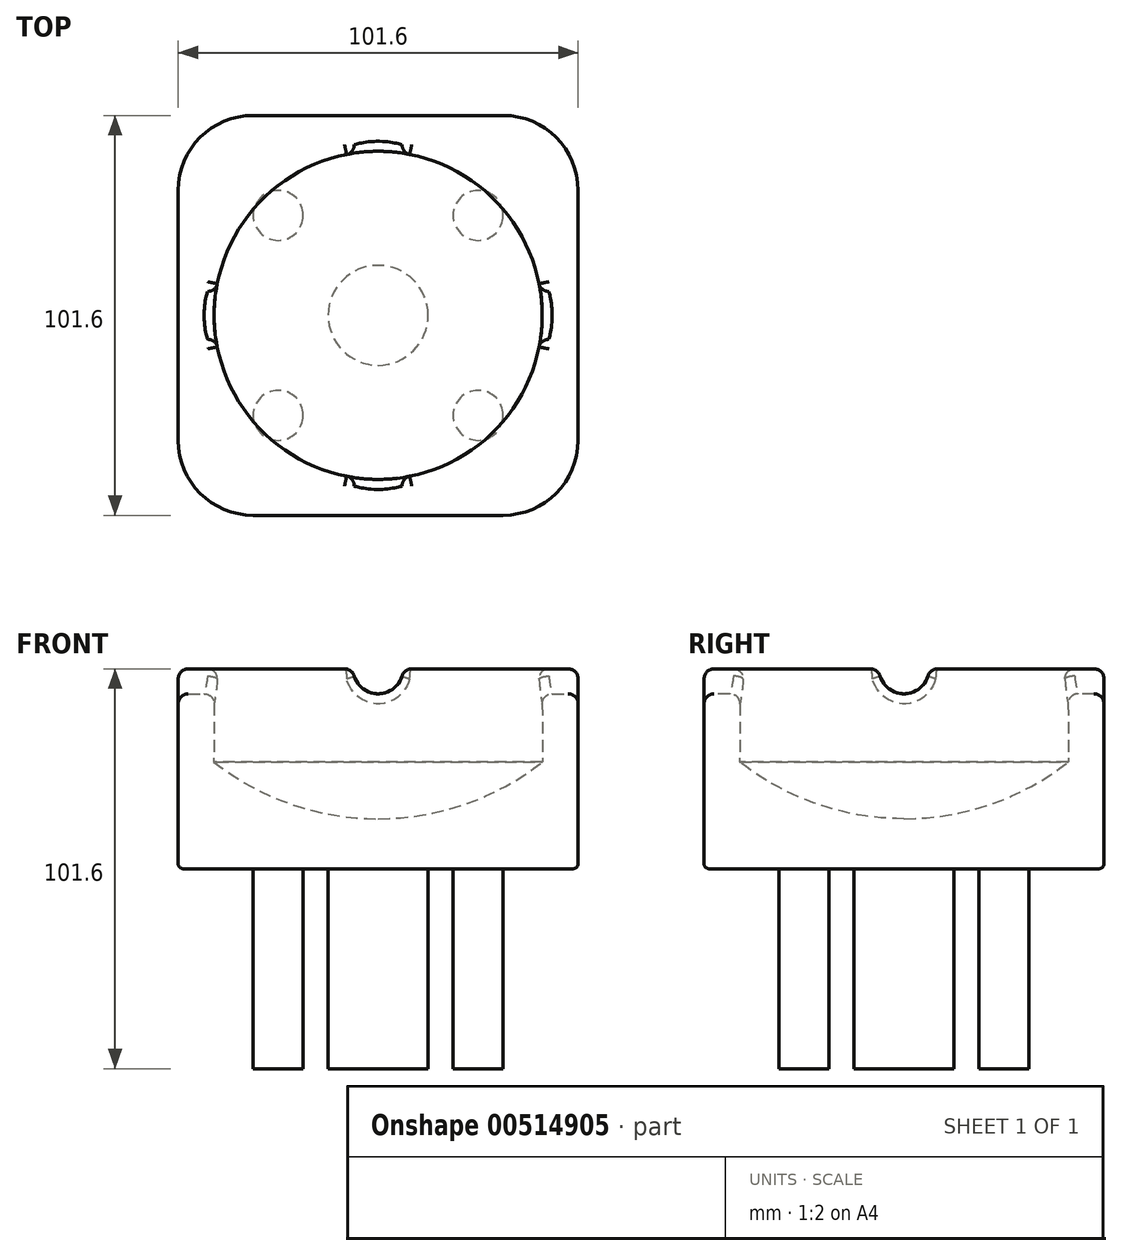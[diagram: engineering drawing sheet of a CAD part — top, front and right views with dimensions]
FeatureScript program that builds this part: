
annotation { "Feature Type Name" : "Feature", "Feature Type Description" : "" }
export const myFeature = defineFeature(function(context is Context, id is Id, definition is map)
    precondition{}
    {
        {
            var Q0;
            Q0=qCreatedBy(makeId("Top.planeOp"),FACE);
            var sketch = newSketch(context, id + "F0", { "sketchPlane" : qUnion([Q0])});
            skLineSegment(sketch, "E0.bottom", {"start": v(50.8, -50.8) * mm, "end": v(-50.8, -50.8) * mm});
            skLineSegment(sketch, "E0.top", {"start": v(50.8, 50.8) * mm, "end": v(-50.8, 50.8) * mm});
            skLineSegment(sketch, "E0.left", {"start": v(50.8, -50.8) * mm, "end": v(50.8, 50.8) * mm});
            skLineSegment(sketch, "E0.right", {"start": v(-50.8, -50.8) * mm, "end": v(-50.8, 50.8) * mm});
            skPoint(sketch, "E0.middle", {"position": v(0, 0) * mm});
            skSolve(sketch);
        }
        {
            var Q0;
            Q0 = qSketchRegion(id + "F0", true);
            extrude(context, id + "F1", {"entities" : qUnion([Q0]), "depth" : 50.8 * mm, "offsetDistance" : 25.4 * mm});
        }
        {
            var Q0;
            Q0=qCreatedBy(makeId("Right.planeOp"),FACE);
            var sketch = newSketch(context, id + "F2", { "sketchPlane" : qUnion([Q0])});
            skLineSegment(sketch, "E1", {"start": v(0, 0) * mm, "end": v(0, 27.14) * mm});
            skArc(sketch, "E2", {"start": v(0, 12.7) * mm, "mid": v(22.1, 16.41) * mm, "end": v(41.75, 27.14) * mm});
            skLineSegment(sketch, "E3", {"start": v(0, 27.14) * mm, "end": v(41.75, 27.14) * mm, "construction": true});
            skLineSegment(sketch, "E4", {"start": v(41.6, 56.83) * mm, "end": v(41.75, 27.14) * mm});
            skLineSegment(sketch, "E5", {"start": v(0, 12.7) * mm, "end": v(0, 56.83) * mm});
            skLineSegment(sketch, "E6", {"start": v(0, 56.83) * mm, "end": v(41.6, 56.83) * mm});
            skSolve(sketch);
        }
        {
            var Q0;
            Q0 = qSketchRegion(id + "F2", true);
            var Q1;
            Q1=sQuery(id+"F2.wireOp",EDGE,"E5");
            revolve(context, id + "F3", {"operationType" : NewBodyOperationType.REMOVE, "entities" : qUnion([Q0]), "axis" : qUnion([Q1]), "revolveType" : RevolveType.FULL, "oppositeDirection" : true});
        }
        {
            var Q0;
            Q0=makeQuery(id+"F1.opExtrude","SWEPT_FACE",FACE,{"disambiguationData":[OSD([sQuery(id+"F0.wireOp",EDGE,"E0.bottom")])]});
            var sketch = newSketch(context, id + "F4", { "sketchPlane" : qUnion([Q0])});
            skCircle(sketch, "E7", {"center": v(0, 50.8) * mm, "radius": 6.35 * mm});
            skSolve(sketch);
        }
        {
            var Q0;
            Q0 = qSketchRegion(id + "F4", true);
            extrude(context, id + "F5", {"entities" : qUnion([Q0]), "operationType" : NewBodyOperationType.REMOVE, "oppositeDirection" : true, "depth" : 381 * mm, "offsetDistance" : 25.4 * mm});
        }
        {
            var Q0;
            Q0=makeQuery(id+"F1.opExtrude","SWEPT_FACE",FACE,{"disambiguationData":[OSD([sQuery(id+"F0.wireOp",EDGE,"E0.left")])]});
            var sketch = newSketch(context, id + "F6", { "sketchPlane" : qUnion([Q0])});
            skCircle(sketch, "E8", {"center": v(0, 50.8) * mm, "radius": 6.35 * mm});
            skSolve(sketch);
        }
        {
            var Q0;
            {var subQ0=sQuery(id+"F6.wireOp",EDGE,"E8");var subQ1=makeQuery(id+"F1.opExtrude","CAP_EDGE",EDGE,{"disambiguationData":[OSD([sQuery(id+"F0.wireOp",EDGE,"E0.left")])],"isStart":false});var subQ2=makeQuery(id+"F6.imprint","INTERSECT",VERTEX,{"disambiguationData":[OD(0.0)],"derivedFrom":[subQ1,subQ0]});Q0=makeQuery(id+"F6.imprint","IMPRINT",FACE,{"disambiguationData":[TD([[makeQuery(id+"F6.imprint","IMPRINT",EDGE,{"disambiguationData":[TD([[subQ2,1.0]])],"derivedFrom":subQ0}),1.0]])]});}
            var Q1;
            {var subQ0=sQuery(id+"F6.wireOp",EDGE,"E8");var subQ1=makeQuery(id+"F1.opExtrude","CAP_EDGE",EDGE,{"disambiguationData":[OSD([sQuery(id+"F0.wireOp",EDGE,"E0.left")])],"isStart":false});var subQ2=makeQuery(id+"F6.imprint","INTERSECT",VERTEX,{"disambiguationData":[OD(0.0)],"derivedFrom":[subQ1,subQ0]});Q1=makeQuery(id+"F6.imprint","IMPRINT",FACE,{"disambiguationData":[TD([[makeQuery(id+"F6.imprint","IMPRINT",EDGE,{"disambiguationData":[TD([[subQ2,-1.0]])],"derivedFrom":subQ0}),1.0]])]});}
            extrude(context, id + "F7", {"entities" : qUnion([Q0, Q1]), "operationType" : NewBodyOperationType.REMOVE, "oppositeDirection" : true, "depth" : 127 * mm, "offsetDistance" : 25.4 * mm});
        }
        {
            var Q0;
            Q0=makeQuery(id+"F1.opExtrude","SWEPT_EDGE",EDGE,{"disambiguationData":[OSD([sQuery(id+"F0.wireOp",EDGE,"E0.bottom"),sQuery(id+"F0.wireOp",EDGE,"E0.left")])]});
            var Q1;
            Q1=makeQuery(id+"F1.opExtrude","SWEPT_EDGE",EDGE,{"disambiguationData":[OSD([sQuery(id+"F0.wireOp",EDGE,"E0.top"),sQuery(id+"F0.wireOp",EDGE,"E0.left")])]});
            var Q2;
            Q2=makeQuery(id+"F1.opExtrude","SWEPT_EDGE",EDGE,{"disambiguationData":[OSD([sQuery(id+"F0.wireOp",EDGE,"E0.top"),sQuery(id+"F0.wireOp",EDGE,"E0.right")])]});
            var Q3;
            Q3=makeQuery(id+"F1.opExtrude","SWEPT_EDGE",EDGE,{"disambiguationData":[OSD([sQuery(id+"F0.wireOp",EDGE,"E0.bottom"),sQuery(id+"F0.wireOp",EDGE,"E0.right")])]});
            fillet(context, id + "F8", {"entities" : qUnion([Q0, Q1, Q2, Q3]), "radius" : 19.05 * mm, "tangentPropagation" : true, "allowEdgeOverflow" : false});
        }
        {
            var Q0;
            {var subQ0=sQuery(id+"F0.wireOp",EDGE,"E0.bottom");var subQ1=makeQuery(id+"F1.opExtrude","SWEPT_FACE",FACE,{"disambiguationData":[OSD([subQ0])]});var subQ3=sQuery(id+"F0.wireOp",EDGE,"E0.right");var subQ4=sQuery(id+"F0.wireOp",EDGE,"E0.top");var subQ5=makeQuery(id+"F1.opExtrude","CAP_FACE",FACE,{"disambiguationData":[OSD([subQ0,subQ4,sQuery(id+"F0.wireOp",EDGE,"E0.left"),subQ3])],"isStart":false});var subQ7=makeQuery(id+"F1.opExtrude","SWEPT_FACE",FACE,{"disambiguationData":[OSD([subQ3])]});Q0=makeQuery(id+"F8.opFillet","BLEND_EDGE",EDGE,{"blendedFrom":[makeQuery(id+"F1.opExtrude","SWEPT_EDGE",EDGE,{"disambiguationData":[OSD([subQ0,subQ3])]}),makeQuery(id+"F7.boolean.opBoolean","SPLIT",FACE,{"disambiguationData":[TD([subQ1])],"derivedFrom":makeQuery(id+"F5.boolean.opBoolean","SPLIT",FACE,{"disambiguationData":[TD([subQ7])],"derivedFrom":subQ5})})],"blendedInto":[makeQuery(id+"F7.boolean.opBoolean","SPLIT",FACE,{"disambiguationData":[TD([subQ1])],"derivedFrom":makeQuery(id+"F5.boolean.opBoolean","SPLIT",FACE,{"disambiguationData":[TD([subQ7])],"derivedFrom":subQ5})})]});}
            var Q1;
            {var subQ0=sQuery(id+"F0.wireOp",EDGE,"E0.right");var subQ1=sQuery(id+"F0.wireOp",EDGE,"E0.top");var subQ2=sQuery(id+"F0.wireOp",EDGE,"E0.bottom");var subQ3=makeQuery(id+"F1.opExtrude","CAP_FACE",FACE,{"disambiguationData":[OSD([subQ2,subQ1,sQuery(id+"F0.wireOp",EDGE,"E0.left"),subQ0])],"isStart":false});var subQ4=makeQuery(id+"F1.opExtrude","SWEPT_FACE",FACE,{"disambiguationData":[OSD([subQ1])]});var subQ7=makeQuery(id+"F1.opExtrude","SWEPT_FACE",FACE,{"disambiguationData":[OSD([subQ0])]});Q1=makeQuery(id+"F8.opFillet","BLEND_EDGE",EDGE,{"blendedFrom":[makeQuery(id+"F1.opExtrude","SWEPT_EDGE",EDGE,{"disambiguationData":[OSD([subQ1,subQ0])]}),makeQuery(id+"F7.boolean.opBoolean","SPLIT",FACE,{"disambiguationData":[TD([subQ4])],"derivedFrom":makeQuery(id+"F5.boolean.opBoolean","SPLIT",FACE,{"disambiguationData":[TD([subQ7])],"derivedFrom":subQ3})})],"blendedInto":[makeQuery(id+"F7.boolean.opBoolean","SPLIT",FACE,{"disambiguationData":[TD([subQ4])],"derivedFrom":makeQuery(id+"F5.boolean.opBoolean","SPLIT",FACE,{"disambiguationData":[TD([subQ7])],"derivedFrom":subQ3})})]});}
            var Q2;
            {var subQ1=sQuery(id+"F0.wireOp",EDGE,"E0.left");var subQ2=sQuery(id+"F0.wireOp",EDGE,"E0.top");var subQ3=sQuery(id+"F0.wireOp",EDGE,"E0.bottom");var subQ4=makeQuery(id+"F1.opExtrude","CAP_FACE",FACE,{"disambiguationData":[OSD([subQ3,subQ2,subQ1,sQuery(id+"F0.wireOp",EDGE,"E0.right")])],"isStart":false});var subQ5=makeQuery(id+"F1.opExtrude","SWEPT_FACE",FACE,{"disambiguationData":[OSD([subQ2])]});var subQ7=makeQuery(id+"F1.opExtrude","SWEPT_FACE",FACE,{"disambiguationData":[OSD([subQ1])]});Q2=makeQuery(id+"F8.opFillet","BLEND_EDGE",EDGE,{"blendedFrom":[makeQuery(id+"F1.opExtrude","SWEPT_EDGE",EDGE,{"disambiguationData":[OSD([subQ2,subQ1])]}),makeQuery(id+"F7.boolean.opBoolean","SPLIT",FACE,{"disambiguationData":[TD([subQ5])],"derivedFrom":makeQuery(id+"F5.boolean.opBoolean","SPLIT",FACE,{"disambiguationData":[TD([subQ7])],"derivedFrom":subQ4})})],"blendedInto":[makeQuery(id+"F7.boolean.opBoolean","SPLIT",FACE,{"disambiguationData":[TD([subQ5])],"derivedFrom":makeQuery(id+"F5.boolean.opBoolean","SPLIT",FACE,{"disambiguationData":[TD([subQ7])],"derivedFrom":subQ4})})]});}
            var Q3;
            {var subQ0=sQuery(id+"F0.wireOp",EDGE,"E0.bottom");var subQ1=makeQuery(id+"F1.opExtrude","SWEPT_FACE",FACE,{"disambiguationData":[OSD([subQ0])]});var subQ3=sQuery(id+"F0.wireOp",EDGE,"E0.left");var subQ4=sQuery(id+"F0.wireOp",EDGE,"E0.top");var subQ5=makeQuery(id+"F1.opExtrude","CAP_FACE",FACE,{"disambiguationData":[OSD([subQ0,subQ4,subQ3,sQuery(id+"F0.wireOp",EDGE,"E0.right")])],"isStart":false});var subQ7=makeQuery(id+"F1.opExtrude","SWEPT_FACE",FACE,{"disambiguationData":[OSD([subQ3])]});Q3=makeQuery(id+"F8.opFillet","BLEND_EDGE",EDGE,{"blendedFrom":[makeQuery(id+"F1.opExtrude","SWEPT_EDGE",EDGE,{"disambiguationData":[OSD([subQ0,subQ3])]}),makeQuery(id+"F7.boolean.opBoolean","SPLIT",FACE,{"disambiguationData":[TD([subQ1])],"derivedFrom":makeQuery(id+"F5.boolean.opBoolean","SPLIT",FACE,{"disambiguationData":[TD([subQ7])],"derivedFrom":subQ5})})],"blendedInto":[makeQuery(id+"F7.boolean.opBoolean","SPLIT",FACE,{"disambiguationData":[TD([subQ1])],"derivedFrom":makeQuery(id+"F5.boolean.opBoolean","SPLIT",FACE,{"disambiguationData":[TD([subQ7])],"derivedFrom":subQ5})})]});}
            var Q4;
            {var subQ0=sQuery(id+"F0.wireOp",EDGE,"E0.top");var subQ1=makeQuery(id+"F1.opExtrude","CAP_FACE",FACE,{"disambiguationData":[OSD([sQuery(id+"F0.wireOp",EDGE,"E0.bottom"),subQ0,sQuery(id+"F0.wireOp",EDGE,"E0.left"),sQuery(id+"F0.wireOp",EDGE,"E0.right")])],"isStart":false});var subQ2=makeQuery(id+"F3.opRevolve","SWEPT_FACE",FACE,{"disambiguationData":[OSD([sQuery(id+"F2.wireOp",EDGE,"E4")])]});Q4=makeQuery(id+"F7.boolean.opBoolean","SPLIT",EDGE,{"disambiguationData":[TD([makeQuery(id+"F5.boolean.opBoolean","COPY",FACE,{"disambiguationData":[TD([makeQuery(id+"F1.opExtrude","SWEPT_FACE",FACE,{"disambiguationData":[OSD([subQ0])]})])],"derivedFrom":makeQuery(id+"F5.opExtrude","SWEPT_FACE",FACE,{"disambiguationData":[OSD([sQuery(id+"F4.wireOp",EDGE,"E7")])]})})])],"derivedFrom":makeQuery(id+"F5.boolean.opBoolean","SPLIT",EDGE,{"disambiguationData":[OD(1.0)],"derivedFrom":makeQuery(id+"F3.boolean.opBoolean","INTERSECT",EDGE,{"derivedFrom":[subQ1,subQ2]})})});}
            var Q5;
            {var subQ0=sQuery(id+"F0.wireOp",EDGE,"E0.top");var subQ1=makeQuery(id+"F1.opExtrude","CAP_FACE",FACE,{"disambiguationData":[OSD([sQuery(id+"F0.wireOp",EDGE,"E0.bottom"),subQ0,sQuery(id+"F0.wireOp",EDGE,"E0.left"),sQuery(id+"F0.wireOp",EDGE,"E0.right")])],"isStart":false});var subQ2=makeQuery(id+"F3.opRevolve","SWEPT_FACE",FACE,{"disambiguationData":[OSD([sQuery(id+"F2.wireOp",EDGE,"E4")])]});Q5=makeQuery(id+"F7.boolean.opBoolean","SPLIT",EDGE,{"disambiguationData":[TD([makeQuery(id+"F5.boolean.opBoolean","COPY",FACE,{"disambiguationData":[TD([makeQuery(id+"F1.opExtrude","SWEPT_FACE",FACE,{"disambiguationData":[OSD([subQ0])]})])],"derivedFrom":makeQuery(id+"F5.opExtrude","SWEPT_FACE",FACE,{"disambiguationData":[OSD([sQuery(id+"F4.wireOp",EDGE,"E7")])]})})])],"derivedFrom":makeQuery(id+"F5.boolean.opBoolean","SPLIT",EDGE,{"disambiguationData":[OD(0.0)],"derivedFrom":makeQuery(id+"F3.boolean.opBoolean","INTERSECT",EDGE,{"derivedFrom":[subQ1,subQ2]})})});}
            var Q6;
            {var subQ0=sQuery(id+"F0.wireOp",EDGE,"E0.bottom");var subQ1=makeQuery(id+"F1.opExtrude","CAP_FACE",FACE,{"disambiguationData":[OSD([subQ0,sQuery(id+"F0.wireOp",EDGE,"E0.top"),sQuery(id+"F0.wireOp",EDGE,"E0.left"),sQuery(id+"F0.wireOp",EDGE,"E0.right")])],"isStart":false});var subQ2=makeQuery(id+"F3.opRevolve","SWEPT_FACE",FACE,{"disambiguationData":[OSD([sQuery(id+"F2.wireOp",EDGE,"E4")])]});Q6=makeQuery(id+"F7.boolean.opBoolean","SPLIT",EDGE,{"disambiguationData":[TD([makeQuery(id+"F5.boolean.opBoolean","COPY",FACE,{"disambiguationData":[TD([makeQuery(id+"F1.opExtrude","SWEPT_FACE",FACE,{"disambiguationData":[OSD([subQ0])]})])],"derivedFrom":makeQuery(id+"F5.opExtrude","SWEPT_FACE",FACE,{"disambiguationData":[OSD([sQuery(id+"F4.wireOp",EDGE,"E7")])]})})])],"derivedFrom":makeQuery(id+"F5.boolean.opBoolean","SPLIT",EDGE,{"disambiguationData":[OD(0.0)],"derivedFrom":makeQuery(id+"F3.boolean.opBoolean","INTERSECT",EDGE,{"derivedFrom":[subQ1,subQ2]})})});}
            var Q7;
            {var subQ0=sQuery(id+"F0.wireOp",EDGE,"E0.bottom");var subQ1=makeQuery(id+"F1.opExtrude","CAP_FACE",FACE,{"disambiguationData":[OSD([subQ0,sQuery(id+"F0.wireOp",EDGE,"E0.top"),sQuery(id+"F0.wireOp",EDGE,"E0.left"),sQuery(id+"F0.wireOp",EDGE,"E0.right")])],"isStart":false});var subQ2=makeQuery(id+"F3.opRevolve","SWEPT_FACE",FACE,{"disambiguationData":[OSD([sQuery(id+"F2.wireOp",EDGE,"E4")])]});Q7=makeQuery(id+"F7.boolean.opBoolean","SPLIT",EDGE,{"disambiguationData":[TD([makeQuery(id+"F5.boolean.opBoolean","COPY",FACE,{"disambiguationData":[TD([makeQuery(id+"F1.opExtrude","SWEPT_FACE",FACE,{"disambiguationData":[OSD([subQ0])]})])],"derivedFrom":makeQuery(id+"F5.opExtrude","SWEPT_FACE",FACE,{"disambiguationData":[OSD([sQuery(id+"F4.wireOp",EDGE,"E7")])]})})])],"derivedFrom":makeQuery(id+"F5.boolean.opBoolean","SPLIT",EDGE,{"disambiguationData":[OD(1.0)],"derivedFrom":makeQuery(id+"F3.boolean.opBoolean","INTERSECT",EDGE,{"derivedFrom":[subQ1,subQ2]})})});}
            var Q8;
            {var subQ0=sQuery(id+"F0.wireOp",EDGE,"E0.right");Q8=makeQuery(id+"F7.boolean.opBoolean","COPY",FACE,{"disambiguationData":[TD([makeQuery(id+"F1.opExtrude","SWEPT_FACE",FACE,{"disambiguationData":[OSD([subQ0])]})])],"derivedFrom":makeQuery(id+"F7.opExtrude","SWEPT_FACE",FACE,{"disambiguationData":[OSD([sQuery(id+"F6.wireOp",EDGE,"E8")])]})});}
            var Q9;
            {var subQ0=sQuery(id+"F0.wireOp",EDGE,"E0.top");Q9=makeQuery(id+"F5.boolean.opBoolean","COPY",FACE,{"disambiguationData":[TD([makeQuery(id+"F1.opExtrude","SWEPT_FACE",FACE,{"disambiguationData":[OSD([subQ0])]})])],"derivedFrom":makeQuery(id+"F5.opExtrude","SWEPT_FACE",FACE,{"disambiguationData":[OSD([sQuery(id+"F4.wireOp",EDGE,"E7")])]})});}
            var Q10;
            {var subQ0=sQuery(id+"F0.wireOp",EDGE,"E0.left");Q10=makeQuery(id+"F7.boolean.opBoolean","COPY",FACE,{"disambiguationData":[TD([makeQuery(id+"F1.opExtrude","SWEPT_FACE",FACE,{"disambiguationData":[OSD([subQ0])]})])],"derivedFrom":makeQuery(id+"F7.opExtrude","SWEPT_FACE",FACE,{"disambiguationData":[OSD([sQuery(id+"F6.wireOp",EDGE,"E8")])]})});}
            var Q11;
            {var subQ0=sQuery(id+"F0.wireOp",EDGE,"E0.bottom");Q11=makeQuery(id+"F5.boolean.opBoolean","COPY",FACE,{"disambiguationData":[TD([makeQuery(id+"F1.opExtrude","SWEPT_FACE",FACE,{"disambiguationData":[OSD([subQ0])]})])],"derivedFrom":makeQuery(id+"F5.opExtrude","SWEPT_FACE",FACE,{"disambiguationData":[OSD([sQuery(id+"F4.wireOp",EDGE,"E7")])]})});}
            fillet(context, id + "F9", {"entities" : qUnion([Q0, Q1, Q2, Q3, Q4, Q5, Q6, Q7, Q8, Q9, Q10, Q11]), "radius" : 2.54 * mm, "tangentPropagation" : true, "allowEdgeOverflow" : false});
        }
        {
            var Q0;
            {var subQ0=sQuery(id+"F0.wireOp",EDGE,"E0.left");var subQ1=sQuery(id+"F0.wireOp",EDGE,"E0.bottom");Q0=makeQuery(id+"F8.opFillet","BLEND_EDGE",EDGE,{"blendedFrom":[makeQuery(id+"F1.opExtrude","SWEPT_EDGE",EDGE,{"disambiguationData":[OSD([subQ1,subQ0])]}),makeQuery(id+"F1.opExtrude","CAP_FACE",FACE,{"disambiguationData":[OSD([subQ1,sQuery(id+"F0.wireOp",EDGE,"E0.top"),subQ0,sQuery(id+"F0.wireOp",EDGE,"E0.right")])],"isStart":true})],"blendedInto":[makeQuery(id+"F1.opExtrude","CAP_FACE",FACE,{"disambiguationData":[OSD([subQ1,sQuery(id+"F0.wireOp",EDGE,"E0.top"),subQ0,sQuery(id+"F0.wireOp",EDGE,"E0.right")])],"isStart":true})]});}
            fillet(context, id + "F10", {"entities" : qUnion([Q0]), "radius" : 1.27 * mm, "tangentPropagation" : true, "allowEdgeOverflow" : false});
        }
        {
            var Q0;
            Q0=qCreatedBy(makeId("Top.planeOp"),FACE);
            var sketch = newSketch(context, id + "F11", { "sketchPlane" : qUnion([Q0])});
            skCircle(sketch, "E9", {"center": v(0, 0) * mm, "radius": 12.7 * mm});
            skCircle(sketch, "E10", {"center": v(-25.4, 25.4) * mm, "radius": 6.35 * mm});
            skCircle(sketch, "E11", {"center": v(-25.4, -25.4) * mm, "radius": 6.35 * mm});
            skCircle(sketch, "E12", {"center": v(25.4, -25.4) * mm, "radius": 6.35 * mm});
            skCircle(sketch, "E13", {"center": v(25.4, 25.4) * mm, "radius": 6.35 * mm});
            skPoint(sketch, "E14.orphan", {"position": v(-50.8, 50.8) * mm});
            skPoint(sketch, "E15.orphan", {"position": v(50.8, 50.8) * mm});
            skPoint(sketch, "E16.orphan", {"position": v(50.8, -50.8) * mm});
            skPoint(sketch, "E17.orphan", {"position": v(-50.8, -50.8) * mm});
            skSolve(sketch);
        }
        {
            var Q0;
            Q0=makeQuery(id+"F11.imprint","IMPRINT",FACE,{"disambiguationData":[TD([[makeQuery(id+"F11.imprint","IMPRINT",EDGE,{"derivedFrom":sQuery(id+"F11.wireOp",EDGE,"E10")}),1.0]])]});
            var Q1;
            Q1=makeQuery(id+"F11.imprint","IMPRINT",FACE,{"disambiguationData":[TD([[makeQuery(id+"F11.imprint","IMPRINT",EDGE,{"derivedFrom":sQuery(id+"F11.wireOp",EDGE,"E11")}),1.0]])]});
            var Q2;
            Q2=makeQuery(id+"F11.imprint","IMPRINT",FACE,{"disambiguationData":[TD([[makeQuery(id+"F11.imprint","IMPRINT",EDGE,{"derivedFrom":sQuery(id+"F11.wireOp",EDGE,"E9")}),1.0]])]});
            var Q3;
            Q3=makeQuery(id+"F11.imprint","IMPRINT",FACE,{"disambiguationData":[TD([[makeQuery(id+"F11.imprint","IMPRINT",EDGE,{"derivedFrom":sQuery(id+"F11.wireOp",EDGE,"E12")}),1.0]])]});
            var Q4;
            Q4=makeQuery(id+"F11.imprint","IMPRINT",FACE,{"disambiguationData":[TD([[makeQuery(id+"F11.imprint","IMPRINT",EDGE,{"derivedFrom":sQuery(id+"F11.wireOp",EDGE,"E13")}),1.0]])]});
            extrude(context, id + "F12", {"entities" : qUnion([Q0, Q1, Q2, Q3, Q4]), "operationType" : NewBodyOperationType.ADD, "depth" : -50.8 * mm, "offsetDistance" : 25.4 * mm});
        }
    });
